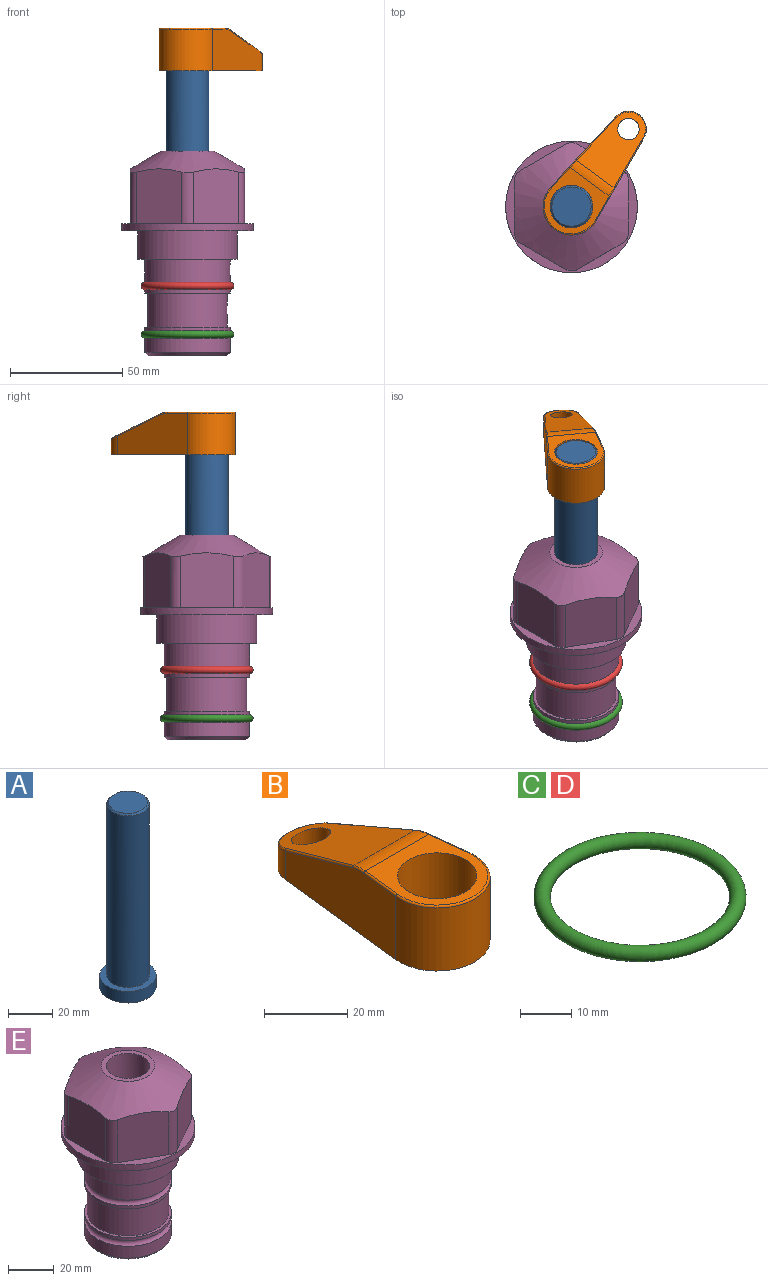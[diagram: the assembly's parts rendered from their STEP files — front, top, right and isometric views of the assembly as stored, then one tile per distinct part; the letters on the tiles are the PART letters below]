
ASSEMBLY  parts=5 mates=3
PART A: 6 faces, bbox 25.4x25.4x101.6 mm
  f0: plane 17.46x17.46mm, normal (0,0,1), area 239.5mm2, adj f5
  f1: plane 25.4x25.4mm, normal (0,0,-1), area 506.7mm2, adj f2
  f2: cylinder r=12.7mm len=25.4mm, axis (0,0,1), area 506.7mm2, adj f1,f3
  f3: plane 25.4x25.4mm, normal (0,0,1), area 221.7mm2, adj f2,f4
  f4: cylinder r=9.53mm len=94.46mm, axis (0,0,1), area 5653mm2, adj f3,f5
  f5: cone r=8.73mm half-angle=45deg, axis (0,0,-1), area 64.4mm2, adj f0,f4
PART B: 44 faces, bbox 27.5x64.5x19.1 mm
  f0: plane 2.3x0.95mm, normal (0,0,-1), area 1mm2, adj f25,f30,f34
  f1: plane 63.5x25.4mm, normal (0,0,-1), area 561.7mm2, adj f2,f3,f4,f5,f6,f7,f19,f20
  f2: cylinder r=12.7mm len=25.4mm, axis (0,0,-1), area 792.2mm2, adj f1,f3,f5,f13
  f3: plane 42.33x18.54mm, normal (0.99,0.11,0), area 647mm2, adj f1,f2,f4,f11,f12,f14
  f4: cylinder r=7.94mm len=15.78mm, axis (0,0,-1), area 158.6mm2, adj f1,f3,f5,f16
  f5: plane 42.33x18.54mm, normal (-0.99,0.11,0), area 647mm2, adj f1,f2,f4,f15,f17,f18
  f6: cylinder r=9.53mm len=19.05mm, axis (0,0,-1), area 1140.1mm2, adj f1,f8
  f7: cylinder r=4.76mm len=10.98mm, axis (0,0,-1), area 276.1mm2, adj f1,f9
  f8: plane 25.83x24.38mm, normal (0,0,1), area 262.2mm2, adj f6,f10,f11,f13,f15
  f9: plane 32.49x20.55mm, normal (0,0.34,0.94), area 489.9mm2, adj f7,f10,f14,f16,f18
  f10: cylinder r=12.7mm len=21.49mm, axis (-1,0,0), area 93.2mm2, adj f8,f9,f12,f17
  f11: cylinder r=0.51mm len=12.34mm, axis (0.11,-0.99,0), area 9.9mm2, adj f3,f8,f12,f13
  f12: bspline ~7.62x1.64mm, area 3.5mm2, adj f3,f10,f11,f14
  f13: torus R=12.19mm, axis (0,0,1), area 33.6mm2, adj f2,f8,f11,f15
  f14: cylinder r=0.51mm len=26.01mm, axis (0.1,-0.93,0.34), area 21.6mm2, adj f3,f9,f12,f16
  f15: cylinder r=0.51mm len=12.34mm, axis (0.11,0.99,0), area 9.9mm2, adj f5,f8,f13,f17
  f16: bspline ~15.78x7.05mm, area 15.7mm2, adj f4,f9,f14,f18
  f17: bspline ~7.62x1.64mm, area 3.5mm2, adj f5,f10,f15,f18
  f18: cylinder r=0.51mm len=26.01mm, axis (0.1,0.93,-0.34), area 21.6mm2, adj f5,f9,f16,f17
  f19: plane 21.6x14.29mm, normal (-0.99,-0.11,0), area 242.6mm2, adj f1,f26,f28,f34,f36,f38
  f20: plane 21.6x14.29mm, normal (0.99,-0.11,0), area 242.6mm2, adj f1,f27,f29,f37,f39,f41
  f21: cylinder r=12.7mm len=14.29mm, axis (0,0,-1), area 173.2mm2, adj f1,f26,f27,f30,f31,f33
  f22: cylinder r=7.94mm len=7.63mm, axis (0,0,-1), area 53.8mm2, adj f1,f28,f29,f42
  f23: plane 2.3x0.95mm, normal (0,0,-1), area 1mm2, adj f25,f33,f37
  f24: plane 17.94x12.32mm, normal (0,-0.34,-0.94), area 191.2mm2, adj f25,f38,f41,f42
  f25: cylinder r=9.53mm len=12.93mm, axis (-1,0,0), area 37.5mm2, adj f0,f23,f24,f31,f36,f39
  f26: cylinder r=1.59mm len=14.29mm, axis (0,0,-1), area 49mm2, adj f1,f19,f21,f32
  f27: cylinder r=1.59mm len=14.29mm, axis (0,0,-1), area 49mm2, adj f1,f20,f21,f35
  f28: cylinder r=1.59mm len=7.28mm, axis (0,0,-1), area 22.1mm2, adj f1,f19,f22,f40
  f29: cylinder r=1.59mm len=7.28mm, axis (0,0,-1), area 22.1mm2, adj f1,f20,f22,f43
  f30: torus R=14.29mm, axis (0,0,1), area 5.8mm2, adj f0,f21,f31,f32
  f31: bspline ~11.06x2.73mm, area 20.8mm2, adj f21,f25,f30,f33
  f32: sphere r=1.59mm, area 5.4mm2, adj f26,f30,f34
  f33: torus R=14.29mm, axis (0,0,1), area 5.8mm2, adj f21,f23,f31,f35
  f34: cylinder r=1.59mm len=1.68mm, axis (-0.11,0.99,0), area 2.4mm2, adj f0,f19,f32,f36
  f35: sphere r=1.59mm, area 5.4mm2, adj f27,f33,f37
  f36: bspline ~5.82x2.33mm, area 7.7mm2, adj f19,f25,f34,f38
  f37: cylinder r=1.59mm len=1.68mm, axis (0.11,0.99,0), area 2.4mm2, adj f20,f23,f35,f39
  f38: cylinder r=1.59mm len=18.33mm, axis (0.1,-0.93,0.34), area 46.7mm2, adj f19,f24,f36,f40
  f39: bspline ~5.82x2.33mm, area 7.7mm2, adj f20,f25,f37,f41
  f40: sphere r=1.59mm, area 3.6mm2, adj f28,f38,f42
  f41: cylinder r=1.59mm len=18.33mm, axis (0.1,0.93,-0.34), area 46.7mm2, adj f20,f24,f39,f43
  f42: bspline ~8.31x1.84mm, area 15.3mm2, adj f22,f24,f40,f43
  f43: sphere r=1.59mm, area 3.6mm2, adj f29,f41,f42
PART C: 1 faces, bbox 44.7x44.7x3.2 mm
  f0: torus R=19.05mm, axis (0,0,1), area 1193.9mm2
PART D: same geometry as C
PART E: 36 faces, bbox 58.7x58.7x91.2 mm
  f0: cylinder r=17.78mm len=35.56mm, axis (0,0,1), area 1670.8mm2, adj f23,f24,f31
  f1: cylinder r=19.05mm len=38.1mm, axis (0,0,1), area 1191.9mm2, adj f26,f27,f30
  f2: plane 58.66x58.66mm, normal (0,0,-1), area 1150.6mm2, adj f3,f28
  f3: cylinder r=29.33mm len=58.66mm, axis (0,0,-1), area 585.1mm2, adj f2,f4
  f4: plane 58.66x58.66mm, normal (0,0,1), area 475.9mm2, adj f3,f5,f6,f7,f8,f9,f10,f11
  f5: plane 24.5x20.32mm, normal (-0.5,0.87,0), area 562.8mm2, adj f4,f15,f16,f17
  f6: plane 24.5x20.32mm, normal (0.5,0.87,0), area 562.8mm2, adj f4,f14,f15,f17
  f7: plane 24.5x23.48mm, normal (1,0,0), area 562.8mm2, adj f4,f13,f14,f17
  f8: plane 24.5x20.32mm, normal (0.5,-0.87,0), area 562.8mm2, adj f4,f12,f13,f17
  f9: plane 24.5x20.32mm, normal (-0.5,-0.87,0), area 562.8mm2, adj f4,f11,f12,f17
  f10: plane 24.5x23.48mm, normal (-1,0,0), area 562.8mm2, adj f4,f11,f16,f17
  f11: cylinder r=5.08mm len=23.01mm, axis (0,0,-1), area 121.2mm2, adj f4,f9,f10,f17
  f12: cylinder r=5.08mm len=23.01mm, axis (0,0,-1), area 121.2mm2, adj f4,f8,f9,f17
  f13: cylinder r=5.08mm len=23.01mm, axis (0,0,-1), area 121.2mm2, adj f4,f7,f8,f17
  f14: cylinder r=5.08mm len=23.01mm, axis (0,0,-1), area 121.2mm2, adj f4,f6,f7,f17
  f15: cylinder r=5.08mm len=23.01mm, axis (0,0,-1), area 121.2mm2, adj f4,f5,f6,f17
  f16: cylinder r=5.08mm len=23.01mm, axis (0,0,-1), area 121.2mm2, adj f4,f5,f10,f17
  f17: cone r=11.73mm half-angle=60deg, axis (0,0,-1), area 2071.8mm2, adj f5,f6,f7,f8,f9,f10,f11,f12
  f18: plane 23.46x23.46mm, normal (0,0,1), area 147.4mm2, adj f17,f35
  f19: plane 34.93x34.93mm, normal (0,0,-1), area 958mm2, adj f29
  f20: cylinder r=19.05mm len=38.1mm, axis (0,0,1), area 760.1mm2, adj f21,f29
  f21: torus R=19.05mm, axis (0,0,1), area 565.3mm2, adj f20,f22
  f22: cylinder r=19.05mm len=38.1mm, axis (0,0,1), area 190mm2, adj f21,f23
  f23: plane 38.1x38.1mm, normal (0,0,1), area 146.9mm2, adj f0,f22
  f24: plane 38.1x38.1mm, normal (0,0,-1), area 146.9mm2, adj f0,f25
  f25: cylinder r=19.05mm len=38.1mm, axis (0,0,1), area 190mm2, adj f24,f26
  f26: torus R=19.05mm, axis (0,0,1), area 565.3mm2, adj f1,f25
  f27: plane 44.45x44.45mm, normal (0,0,-1), area 411.7mm2, adj f1,f28
  f28: cylinder r=22.23mm len=44.45mm, axis (0,0,1), area 1773.5mm2, adj f2,f27
  f29: cone r=19.05mm half-angle=45deg, axis (0,0,1), area 257.5mm2, adj f19,f20
  f30: cylinder r=3.17mm len=6.75mm, axis (-1,0,0), area 128mm2, adj f1,f33
  f31: cylinder r=3.17mm len=6.35mm, axis (-1,0,0), area 102.5mm2, adj f0,f33
  f32: plane 25.4x25.4mm, normal (0,0,1), area 506.7mm2, adj f33
  f33: cylinder r=12.7mm len=66.42mm, axis (0,0,-1), area 5236.2mm2, adj f30,f31,f32,f34
  f34: cone r=9.53mm half-angle=30deg, axis (0,0,-1), area 443.4mm2, adj f33,f35
  f35: cylinder r=9.53mm len=19.05mm, axis (0,0,-1), area 849mm2, adj f18,f34
PLACE A rot(axis=(0,0,1),53.7deg) t=(0,0,16.65)mm
PLACE B rot(axis=(0,0,-1),36.3deg) t=(0,0,71.26)mm
PLACE C t=(0,0,-21.59)mm
PLACE D at identity
PLACE E at identity fixed
MATE fastened C.f0 <-> E.f0  axis (0,0,1) through (0,0,-46.1)mm
MATE cylindrical A.f2 <-> E.f0  axis (0,0,1) through (0,0,42.29)mm
MATE fastened B.f2 <-> A.f2  axis (0,0,1) through (0,0,90.31)mm
